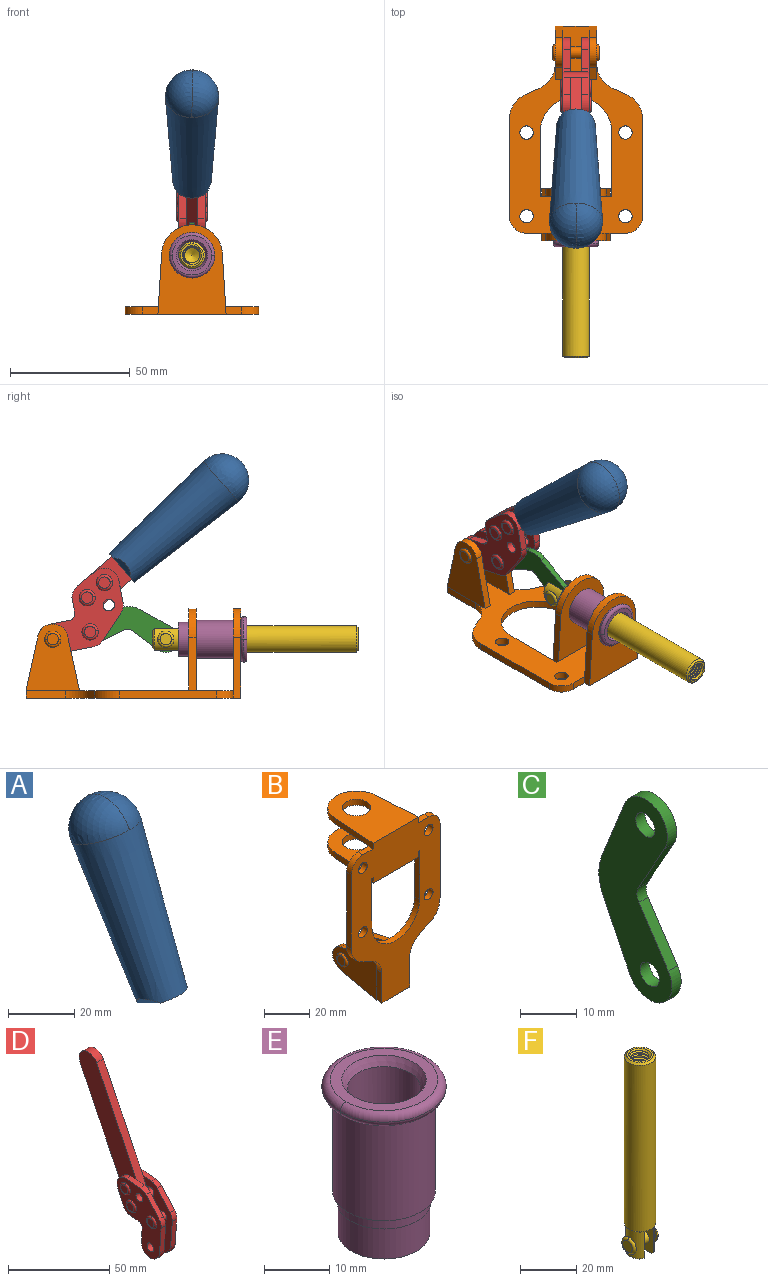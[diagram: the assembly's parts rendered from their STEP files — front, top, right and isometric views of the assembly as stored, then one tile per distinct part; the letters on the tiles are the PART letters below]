
ASSEMBLY  parts=6 mates=6
PART A: 11 faces, bbox 22.3x42.6x64.5 mm
  f0: sphere r=11.13mm, area 411.4mm2, adj f1,f8
  f1: cone r=11.11mm half-angle=3.3deg, axis (0,0.44,0.9), area 3251.8mm2, adj f0,f7,f8,f9,f10
  f2: cylinder r=6.16mm len=11.7mm, axis (1,0,0), area 89.5mm2, adj f3,f4,f5,f6
  f3: plane 60.23x36.75mm, normal (-1,0,0), area 763.6mm2, adj f2,f4,f6,f10
  f4: plane 51.37x25.05mm, normal (0,0.9,-0.44), area 264.2mm2, adj f2,f3,f5,f10
  f5: plane 60.23x36.75mm, normal (1,0,0), area 763.6mm2, adj f2,f4,f6,f10
  f6: plane 51.37x25.05mm, normal (0,-0.9,0.44), area 264.2mm2, adj f2,f3,f5,f10
  f7: plane 9.95x5.95mm, normal (0.71,-0.31,-0.64), area 25.8mm2, adj f1,f10
  f8: sphere r=11.13mm, area 411.4mm2, adj f0,f1
  f9: plane 9.95x5.95mm, normal (-0.71,-0.31,-0.64), area 25.8mm2, adj f1,f10
  f10: plane 14.27x11.38mm, normal (0,-0.44,-0.9), area 106.7mm2, adj f1,f3,f4,f5,f6,f7,f9
PART B: 55 faces, bbox 55.7x37.4x89.8 mm
  f0: torus R=2.41mm, axis (-1,0,0), area 15mm2, adj f11,f15,f25
  f1: torus R=2.41mm, axis (-1,0,0), area 15mm2, adj f10,f12,f22
  f2: cylinder r=2.78mm len=5.56mm, axis (0,-1,0), area 54.2mm2, adj f30,f54
  f3: cylinder r=14.99mm len=29.97mm, axis (0,-1,0), area 145.9mm2, adj f30,f49,f53,f54
  f4: cylinder r=2.78mm len=5.56mm, axis (0,-1,0), area 54.2mm2, adj f30,f54
  f5: cylinder r=2.78mm len=5.56mm, axis (0,-1,0), area 54.2mm2, adj f30,f54
  f6: cylinder r=2.78mm len=5.56mm, axis (0,-1,0), area 54.2mm2, adj f30,f54
  f7: cylinder r=6.35mm len=12.7mm, axis (0,0,1), area 123.6mm2, adj f27,f51
  f8: cylinder r=6.35mm len=12.7mm, axis (0,0,-1), area 124.7mm2, adj f21,f35
  f9: cylinder r=2.41mm len=11.18mm, axis (-1,0,0), area 169.4mm2, adj f16,f19
  f10: plane 4.83x4.83mm, normal (1,0,0), area 18.3mm2, adj f1,f12
  f11: plane 4.83x4.83mm, normal (-1,0,0), area 18.3mm2, adj f0,f15
  f12: torus R=2.41mm, axis (-1,0,0), area 15mm2, adj f1,f10,f22
  f13: cylinder r=6.35mm len=12.41mm, axis (1,0,0), area 53.4mm2, adj f18,f19,f22,f23
  f14: cylinder r=6.35mm len=12.41mm, axis (-1,0,0), area 53.4mm2, adj f16,f17,f24,f25
  f15: torus R=2.41mm, axis (-1,0,0), area 15mm2, adj f0,f11,f25
  f16: plane 27.86x22.35mm, normal (1,0,0), area 425.4mm2, adj f9,f14,f17,f24,f30
  f17: plane 22.86x4.97mm, normal (0,0.21,0.98), area 72.5mm2, adj f14,f16,f25,f30
  f18: plane 22.86x4.97mm, normal (0,0.21,0.98), area 72.5mm2, adj f13,f19,f22,f30
  f19: plane 27.86x22.35mm, normal (-1,0,0), area 425.4mm2, adj f9,f13,f18,f23,f30
  f20: cylinder r=12.7mm len=25.35mm, axis (0,0,-1), area 119.8mm2, adj f21,f34,f35,f36
  f21: plane 34.21x28.07mm, normal (0,0,-1), area 702.4mm2, adj f8,f20,f30,f34,f36
  f22: plane 27.96x22.45mm, normal (1,0,0), area 407.2mm2, adj f1,f12,f13,f18,f23,f30,f42,f43
  f23: plane 22.86x4.97mm, normal (0,0.21,-0.98), area 72.5mm2, adj f13,f19,f22,f44
  f24: plane 22.86x4.97mm, normal (0,0.21,-0.98), area 72.5mm2, adj f14,f16,f25,f44
  f25: plane 27.86x22.35mm, normal (-1,0,0), area 407.1mm2, adj f0,f14,f15,f17,f24,f30,f45,f46
  f26: plane 3.1x0.95mm, normal (0,0,-1), area 2.7mm2, adj f30,f49,f50,f54
  f27: plane 34.21x28.07mm, normal (0,0,1), area 702.4mm2, adj f7,f28,f30,f50,f52
  f28: cylinder r=12.7mm len=25.35mm, axis (0,0,1), area 118.8mm2, adj f27,f50,f51,f52
  f29: plane 3.1x0.95mm, normal (0,0,-1), area 2.7mm2, adj f30,f52,f53,f54
  f30: plane 86.54x55.63mm, normal (0,1,0), area 2362.9mm2, adj f2,f3,f4,f5,f6,f16,f17,f18
  f31: plane 40.56x3.1mm, normal (-1,0,0), area 125.7mm2, adj f30,f32,f48,f54
  f32: cylinder r=7.11mm len=7.11mm, axis (0,-1,0), area 34.6mm2, adj f30,f31,f33,f54
  f33: plane 6.67x3.1mm, normal (0,0,1), area 20.4mm2, adj f30,f32,f34,f54
  f34: plane 25.39x3.13mm, normal (-1,0.06,0), area 79.5mm2, adj f20,f21,f33,f35,f54
  f35: plane 37.31x28.45mm, normal (0,0,1), area 789.9mm2, adj f8,f20,f34,f36,f54
  f36: plane 25.39x3.13mm, normal (1,0.06,0), area 79.5mm2, adj f20,f21,f35,f37,f54
  f37: plane 6.67x3.1mm, normal (0,0,1), area 20.4mm2, adj f30,f36,f38,f54
  f38: cylinder r=7.11mm len=7.11mm, axis (0,-1,0), area 34.6mm2, adj f30,f37,f39,f54
  f39: plane 40.56x3.1mm, normal (1,0,0), area 125.7mm2, adj f30,f38,f40,f54
  f40: cylinder r=11.18mm len=10.16mm, axis (0,-1,0), area 39.5mm2, adj f30,f39,f41,f54
  f41: plane 6.09x3.1mm, normal (0.42,0,-0.91), area 20.8mm2, adj f30,f40,f42,f54
  f42: cylinder r=11.18mm len=9.41mm, axis (0,-1,0), area 37.2mm2, adj f22,f30,f41,f43,f54
  f43: plane 16.5x3.1mm, normal (1,0,0), area 51.1mm2, adj f22,f42,f44,f54
  f44: plane 17.37x3.1mm, normal (0,0,-1), area 53.8mm2, adj f23,f24,f30,f43,f45,f54
  f45: plane 16.5x3.1mm, normal (-1,0,0), area 51.1mm2, adj f25,f44,f46,f54
  f46: cylinder r=11.18mm len=9.41mm, axis (0,-1,0), area 37.2mm2, adj f25,f30,f45,f47,f54
  f47: plane 6.09x3.1mm, normal (-0.42,0,-0.91), area 20.8mm2, adj f30,f46,f48,f54
  f48: cylinder r=11.18mm len=10.16mm, axis (0,-1,0), area 39.5mm2, adj f30,f31,f47,f54
  f49: plane 26.54x3.1mm, normal (-1,0,0), area 82.3mm2, adj f3,f26,f30,f54
  f50: plane 25.39x3.1mm, normal (1,0.06,0), area 78.8mm2, adj f26,f27,f28,f51,f54
  f51: plane 37.31x28.45mm, normal (0,0,-1), area 789.9mm2, adj f7,f28,f50,f52,f54
  f52: plane 25.39x3.1mm, normal (-1,0.06,0), area 78.8mm2, adj f27,f28,f29,f51,f54
  f53: plane 26.54x3.1mm, normal (1,0,0), area 82.3mm2, adj f3,f29,f30,f54
  f54: plane 89.66x55.63mm, normal (0,-1,0), area 2678.5mm2, adj f2,f3,f4,f5,f6,f26,f29,f31
PART C: 12 faces, bbox 2.3x18.2x42.8 mm
  f0: cylinder r=2.4mm len=4.8mm, axis (1,0,0), area 34.9mm2, adj f4,f11
  f1: cylinder r=10.41mm len=8.47mm, axis (1,0,0), area 20.2mm2, adj f4,f9,f10,f11
  f2: cylinder r=3.05mm len=3.16mm, axis (1,0,0), area 7.7mm2, adj f4,f6,f7,f11
  f3: cylinder r=2.4mm len=4.8mm, axis (1,0,0), area 34.9mm2, adj f4,f11
  f4: plane 42.81x18.23mm, normal (-1,0,0), area 414.1mm2, adj f0,f1,f2,f3,f5,f6,f7,f8
  f5: cylinder r=5.54mm len=10.67mm, axis (1,0,0), area 41.8mm2, adj f4,f6,f10,f11
  f6: plane 11.66x6.53mm, normal (0,-0.87,-0.49), area 30.9mm2, adj f2,f4,f5,f11
  f7: plane 11.17x7.33mm, normal (0,-0.84,0.55), area 30.9mm2, adj f2,f4,f8,f11
  f8: cylinder r=5.54mm len=10.51mm, axis (1,0,0), area 41.8mm2, adj f4,f7,f9,f11
  f9: plane 13.67x6.67mm, normal (0,0.9,-0.44), area 35.1mm2, adj f1,f4,f8,f11
  f10: plane 14.1x5.7mm, normal (0,0.93,0.37), area 35.1mm2, adj f1,f4,f5,f11
  f11: plane 42.81x18.23mm, normal (1,0,0), area 414.1mm2, adj f0,f1,f2,f3,f5,f6,f7,f8
PART D: 59 faces, bbox 12.9x60.2x99.6 mm
  f0: torus R=2.39mm, axis (-1,0,0), area 14.9mm2, adj f20,f43,f51
  f1: torus R=2.39mm, axis (-1,0,0), area 14.9mm2, adj f19,f42,f51
  f2: torus R=2.39mm, axis (-1,0,0), area 14.9mm2, adj f18,f35,f51
  f3: torus R=2.39mm, axis (-1,0,0), area 14.9mm2, adj f14,f17,f23
  f4: torus R=2.39mm, axis (-1,0,0), area 14.9mm2, adj f13,f16,f23
  f5: torus R=2.39mm, axis (-1,0,0), area 14.9mm2, adj f12,f15,f23
  f6: cylinder r=2.39mm len=4.78mm, axis (1,0,0), area 46.5mm2, adj f48,f50,f51
  f7: cylinder r=2.39mm len=4.78mm, axis (1,0,0), area 46.5mm2, adj f50,f51
  f8: cylinder r=6.35mm len=12.68mm, axis (1,0,0), area 61.8mm2, adj f38,f39,f50,f51
  f9: cylinder r=2.39mm len=4.78mm, axis (-1,0,0), area 70.5mm2, adj f46,f50
  f10: cylinder r=2.39mm len=4.78mm, axis (-1,0,0), area 46.5mm2, adj f23,f45,f46
  f11: cylinder r=2.39mm len=4.78mm, axis (-1,0,0), area 46.5mm2, adj f23,f46
  f12: plane 4.78x4.78mm, normal (1,0,0), area 17.9mm2, adj f5,f15
  f13: plane 4.78x4.78mm, normal (1,0,0), area 17.9mm2, adj f4,f16
  f14: plane 4.78x4.78mm, normal (1,0,0), area 17.9mm2, adj f3,f17
  f15: torus R=2.39mm, axis (-1,0,0), area 14.9mm2, adj f5,f12,f23
  f16: torus R=2.39mm, axis (-1,0,0), area 14.9mm2, adj f4,f13,f23
  f17: torus R=2.39mm, axis (-1,0,0), area 14.9mm2, adj f3,f14,f23
  f18: plane 4.78x4.78mm, normal (-1,0,0), area 17.9mm2, adj f2,f35
  f19: plane 4.78x4.78mm, normal (-1,0,0), area 17.9mm2, adj f1,f42
  f20: plane 4.78x4.78mm, normal (-1,0,0), area 17.9mm2, adj f0,f43
  f21: plane 2.26x0.2mm, normal (1,0,0), area 0.2mm2, adj f31,f44
  f22: plane 2.26x0.2mm, normal (-1,0,0), area 0.2mm2, adj f41,f44
  f23: plane 39.37x30.77mm, normal (1,0,0), area 565.5mm2, adj f3,f4,f5,f10,f11,f15,f16,f17
  f24: cylinder r=6.1mm len=4.15mm, axis (-1,0,0), area 14.7mm2, adj f23,f25,f32,f46
  f25: plane 10.25x9.01mm, normal (0,-0.75,0.66), area 42.3mm2, adj f23,f24,f26,f46
  f26: cylinder r=6.35mm len=4.64mm, axis (-1,0,0), area 15.6mm2, adj f23,f25,f27,f46
  f27: plane 15.84x3.1mm, normal (0,-1,-0.07), area 49.2mm2, adj f23,f26,f28,f46
  f28: cylinder r=6.35mm len=12.68mm, axis (-1,0,0), area 61.8mm2, adj f23,f27,f29,f46
  f29: plane 8.11x3.1mm, normal (0,1,0.07), area 25.2mm2, adj f23,f28,f30,f46
  f30: cylinder r=3.05mm len=3.25mm, axis (-1,0,0), area 14.8mm2, adj f23,f29,f31,f46
  f31: plane 5.99x3.1mm, normal (0,0.07,-1), area 18.6mm2, adj f21,f23,f30,f44,f46
  f32: plane 9.5x3.1mm, normal (0,-0.07,1), area 29.5mm2, adj f23,f24,f33,f46,f47
  f33: cylinder r=6.1mm len=8.63mm, axis (-1,0,0), area 39.1mm2, adj f23,f32,f34,f47
  f34: plane 8.65x3.96mm, normal (0,0.91,-0.42), area 29.5mm2, adj f23,f33,f44,f47
  f35: torus R=2.39mm, axis (-1,0,0), area 14.9mm2, adj f2,f18,f51
  f36: plane 10.25x9.01mm, normal (0,-0.75,0.66), area 42.3mm2, adj f37,f49,f50,f51
  f37: cylinder r=6.35mm len=4.64mm, axis (1,0,0), area 15.6mm2, adj f36,f38,f50,f51
  f38: plane 15.84x3.1mm, normal (0,-1,-0.07), area 49.2mm2, adj f8,f37,f50,f51
  f39: plane 8.11x3.1mm, normal (0,1,0.07), area 25.2mm2, adj f8,f40,f50,f51
  f40: cylinder r=3.05mm len=3.25mm, axis (1,0,0), area 14.8mm2, adj f39,f41,f50,f51
  f41: plane 5.99x3.1mm, normal (0,0.07,-1), area 18.6mm2, adj f22,f40,f44,f50,f51
  f42: torus R=2.39mm, axis (-1,0,0), area 14.9mm2, adj f1,f19,f51
  f43: torus R=2.39mm, axis (-1,0,0), area 14.9mm2, adj f0,f20,f51
  f44: cylinder r=6.35mm len=12.12mm, axis (-1,0,0), area 128.9mm2, adj f21,f22,f23,f31,f34,f41,f46,f47
  f45: plane 2.65x1.35mm, normal (1,0,0), area 1mm2, adj f10,f55
  f46: plane 39.08x20.42mm, normal (-1,0,0), area 412.5mm2, adj f9,f10,f11,f24,f25,f26,f27,f28
  f47: plane 77.62x39.82mm, normal (1,0,0), area 850mm2, adj f32,f33,f34,f44,f53,f54,f55
  f48: plane 2.65x1.35mm, normal (-1,0,0), area 1mm2, adj f6,f55
  f49: cylinder r=6.1mm len=4.15mm, axis (1,0,0), area 14.7mm2, adj f36,f50,f51,f56
  f50: plane 39.08x20.42mm, normal (1,0,0), area 412.5mm2, adj f6,f7,f8,f9,f36,f37,f38,f39
  f51: plane 39.37x30.77mm, normal (-1,0,0), area 565.5mm2, adj f0,f1,f2,f6,f7,f8,f35,f36
  f52: plane 8.65x3.96mm, normal (0,0.91,-0.42), area 29.5mm2, adj f44,f51,f57,f58
  f53: plane 68.49x33.4mm, normal (0,0.9,-0.44), area 358.1mm2, adj f44,f47,f54,f58
  f54: cylinder r=6.35mm len=12.06mm, axis (1,0,0), area 93.7mm2, adj f47,f53,f55,f58
  f55: plane 68.49x33.4mm, normal (0,-0.9,0.44), area 358.1mm2, adj f44,f45,f46,f47,f48,f50,f54,f58
  f56: plane 9.5x3.1mm, normal (0,-0.07,1), area 29.5mm2, adj f49,f50,f51,f57,f58
  f57: cylinder r=6.1mm len=8.63mm, axis (1,0,0), area 39.1mm2, adj f51,f52,f56,f58
  f58: plane 77.62x39.82mm, normal (-1,0,0), area 850mm2, adj f44,f52,f53,f54,f55,f56,f57
PART E: 15 faces, bbox 20.6x20.6x28.7 mm
  f0: torus R=8.26mm, axis (0,0,1), area 56.8mm2, adj f1,f10,f12
  f1: torus R=8.26mm, axis (0,0,1), area 56.8mm2, adj f0,f6,f13
  f2: cylinder r=5.59mm len=25.91mm, axis (0,0,1), area 909.6mm2, adj f3,f4
  f3: cone r=6.86mm half-angle=45deg, axis (0,0,-1), area 70.2mm2, adj f2,f14
  f4: cone r=6.47mm half-angle=30deg, axis (0,0,1), area 66.7mm2, adj f2,f13
  f5: cylinder r=7.04mm len=14.07mm, axis (0,0,1), area 252.6mm2, adj f11,f14
  f6: torus R=8.26mm, axis (0,0,1), area 56.8mm2, adj f1,f12,f13
  f7: cylinder r=7.16mm len=14.33mm, axis (0,0,1), area 91.5mm2, adj f9,f11
  f8: cylinder r=7.86mm len=18.42mm, axis (0,0,1), area 909.6mm2, adj f9,f10
  f9: plane 15.72x15.72mm, normal (0,0,-1), area 33mm2, adj f7,f8
  f10: plane 16.51x16.51mm, normal (0,0,-1), area 19.9mm2, adj f0,f8,f12
  f11: plane 14.33x14.33mm, normal (0,0,-1), area 5.7mm2, adj f5,f7
  f12: torus R=8.26mm, axis (0,0,1), area 56.8mm2, adj f0,f6,f10
  f13: plane 16.51x16.51mm, normal (0,0,1), area 82.7mm2, adj f1,f4,f6
  f14: plane 14.07x14.07mm, normal (0,0,-1), area 7.8mm2, adj f3,f5
PART F: 48 faces, bbox 12.6x11.1x86.1 mm
  f0: torus R=2.41mm, axis (-1,0,0), area 15mm2, adj f30,f32,f34
  f1: torus R=2.41mm, axis (-1,0,0), area 15mm2, adj f29,f31,f33
  f2: cylinder r=5.54mm len=72.39mm, axis (0,0,1), area 2518.5mm2, adj f3,f4,f42,f43
  f3: cone r=5.54mm half-angle=45deg, axis (0,0,1), area 7.6mm2, adj f2,f5,f41
  f4: cone r=5.54mm half-angle=45deg, axis (0,0,-1), area 34.9mm2, adj f2,f39
  f5: cylinder r=5.08mm len=11.48mm, axis (0,0,1), area 108.3mm2, adj f3,f7,f8,f41
  f6: cylinder r=2.41mm len=4.83mm, axis (-1,0,0), area 71.2mm2, adj f40,f41
  f7: cylinder r=2.41mm len=4.83mm, axis (-1,0,0), area 7.6mm2, adj f5,f34
  f8: cone r=5.08mm half-angle=45deg, axis (0,0,1), area 10.6mm2, adj f5,f37,f41
  f9: cone r=3.98mm half-angle=45deg, axis (0,0,1), area 17.6mm2, adj f27,f39,f45,f46,f47
  f10: cylinder r=2.41mm len=4.83mm, axis (-1,0,0), area 7.6mm2, adj f33,f38
  f11: cylinder r=3.2mm len=6.4mm, axis (0,0,1), area 78.4mm2, adj f12,f28,f44,f45,f47
  f12: cylinder r=3.2mm len=6.4mm, axis (0,0,1), area 10.5mm2, adj f11,f13,f45,f47
  f13: cylinder r=3.2mm len=6.4mm, axis (0,0,1), area 10.5mm2, adj f12,f14,f45,f47
  f14: cylinder r=3.2mm len=6.4mm, axis (0,0,1), area 10.5mm2, adj f13,f15,f45,f47
  f15: cylinder r=3.2mm len=6.4mm, axis (0,0,1), area 10.5mm2, adj f14,f16,f45,f47
  f16: cylinder r=3.2mm len=6.4mm, axis (0,0,1), area 10.5mm2, adj f15,f17,f45,f47
  f17: cylinder r=3.2mm len=6.4mm, axis (0,0,1), area 10.5mm2, adj f16,f18,f45,f47
  f18: cylinder r=3.2mm len=6.4mm, axis (0,0,1), area 10.5mm2, adj f17,f19,f45,f47
  f19: cylinder r=3.2mm len=6.4mm, axis (0,0,1), area 10.5mm2, adj f18,f20,f45,f47
  f20: cylinder r=3.2mm len=6.4mm, axis (0,0,1), area 10.5mm2, adj f19,f21,f45,f47
  f21: cylinder r=3.2mm len=6.4mm, axis (0,0,1), area 10.5mm2, adj f20,f22,f45,f47
  f22: cylinder r=3.2mm len=6.4mm, axis (0,0,1), area 10.5mm2, adj f21,f23,f45,f47
  f23: cylinder r=3.2mm len=6.4mm, axis (0,0,1), area 10.5mm2, adj f22,f24,f45,f47
  f24: cylinder r=3.2mm len=6.4mm, axis (0,0,1), area 10.5mm2, adj f23,f25,f45,f47
  f25: cylinder r=3.2mm len=6.4mm, axis (0,0,1), area 10.5mm2, adj f24,f26,f45,f47
  f26: cylinder r=3.2mm len=6.4mm, axis (0,0,1), area 10.5mm2, adj f25,f27,f45,f47
  f27: cylinder r=3.2mm len=6.4mm, axis (0,0,1), area 7.4mm2, adj f9,f26,f45,f47
  f28: cone r=3.2mm half-angle=60deg, axis (0,0,1), area 37.2mm2, adj f11
  f29: plane 4.83x4.83mm, normal (-1,0,0), area 18.3mm2, adj f1,f31
  f30: plane 4.83x4.83mm, normal (1,0,0), area 18.3mm2, adj f0,f32
  f31: torus R=2.41mm, axis (-1,0,0), area 15mm2, adj f1,f29,f33
  f32: torus R=2.41mm, axis (-1,0,0), area 15mm2, adj f0,f30,f34
  f33: plane 6.83x6.83mm, normal (1,0,0), area 18.3mm2, adj f1,f10,f31
  f34: plane 6.83x6.83mm, normal (-1,0,0), area 18.3mm2, adj f0,f7,f32
  f35: cone r=5.08mm half-angle=45deg, axis (0,0,1), area 10.6mm2, adj f36,f38,f40
  f36: plane 7.25x1.97mm, normal (0,0,-1), area 10mm2, adj f35,f40
  f37: plane 7.25x1.97mm, normal (0,0,-1), area 10mm2, adj f8,f41
  f38: cylinder r=5.08mm len=11.48mm, axis (0,0,1), area 108.3mm2, adj f10,f35,f40,f42
  f39: plane 9.55x9.55mm, normal (0,0,1), area 22mm2, adj f4,f9
  f40: plane 12.76x10.09mm, normal (1,0,0), area 95.7mm2, adj f6,f35,f36,f38,f42,f43
  f41: plane 12.76x10.09mm, normal (-1,0,0), area 95.7mm2, adj f3,f5,f6,f8,f37,f43
  f42: cone r=5.54mm half-angle=45deg, axis (0,0,1), area 7.6mm2, adj f2,f38,f40
  f43: plane 11.07x4.7mm, normal (0,0,-1), area 50.4mm2, adj f2,f40,f41
  f44: plane 0.89x0.62mm, normal (-1,0,0), area 0.3mm2, adj f11,f45,f46,f47
  f45: bspline ~24.8x7.63mm, area 266.6mm2, adj f9,f11,f12,f13,f14,f15,f16,f17
  f46: bspline ~24.87x7.63mm, area 73.6mm2, adj f9,f44,f45,f47
  f47: bspline ~24.98x7.63mm, area 272.5mm2, adj f9,f11,f12,f13,f14,f15,f16,f17
PLACE A rot(axis=(1,0,0),75deg) t=(0,3.86,9.14)mm
PLACE B rot(axis=(1,0,0),90deg) t=(0,9.14,0)mm fixed
PLACE C rot(axis=(1,0,0),97.5deg) t=(0,12.59,2.22)mm
PLACE D rot(axis=(1,0,0),75deg) t=(0,3.86,9.14)mm
PLACE E rot(axis=(1,0,0),90deg) t=(0,9.14,0)mm
PLACE F rot(axis=(1,0,0),90deg) t=(0,9.52,0)mm
MATE revolute D.f7 <-> B.f0  axis (-1,0,0) through (0,41.23,24.61)mm
MATE revolute C.f3 <-> D.f4  axis (1,0,0) through (0,25.65,27.64)mm
MATE fastened E.f2 <-> B.f7  axis (0,-1,0) through (0,-37.25,24.61)mm
MATE slider F.f2 <-> E.f2  axis (0,-1,0) through (0,-49.26,24.61)mm
MATE revolute C.f5 <-> F.f6  axis (1,0,0) through (0,-5.96,24.61)mm
MATE fastened A.f2 <-> D.f54  axis (1,0,0) through (0,-30.66,91.94)mm
